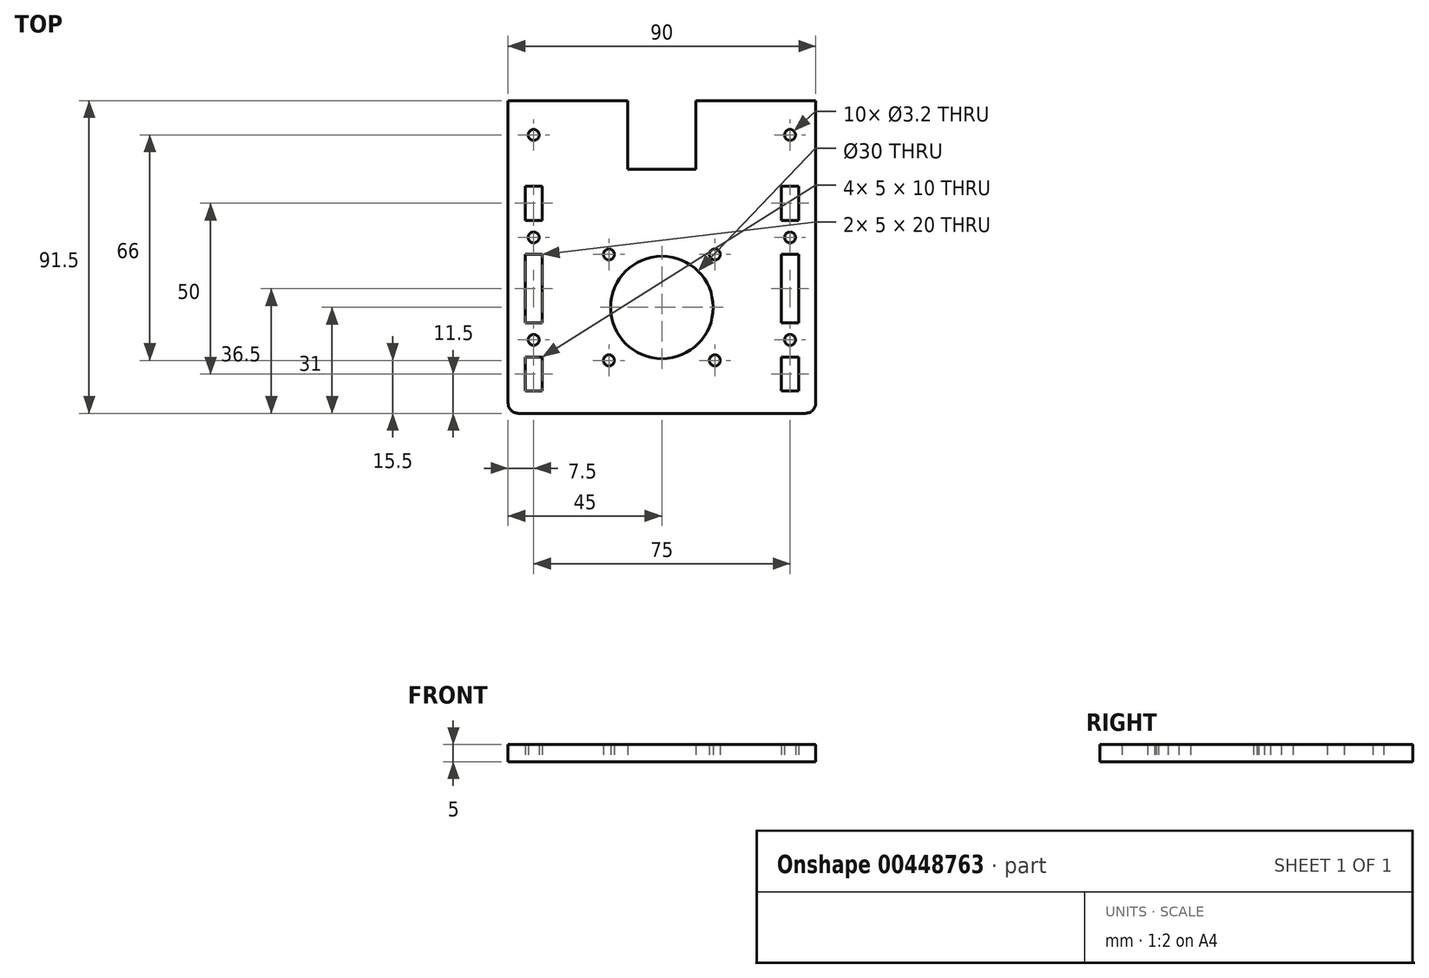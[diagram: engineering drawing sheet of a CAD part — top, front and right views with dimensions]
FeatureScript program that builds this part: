
annotation { "Feature Type Name" : "Feature", "Feature Type Description" : "" }
export const myFeature = defineFeature(function(context is Context, id is Id, definition is map)
    precondition{}
    {
        {
            assignVariable(context, id + "F0", {"name" : "thickness", "anyValue" : 5 * mm});
        }
        {
            var Q0;
            Q0=qCreatedBy(makeId("Top.planeOp"),FACE);
            var sketch = newSketch(context, id + "F1", { "sketchPlane" : qUnion([Q0])});
            skLineSegment(sketch, "E0", {"start": v(0, 0) * mm, "end": v(0, -20) * mm});
            skLineSegment(sketch, "E1", {"start": v(0, -20) * mm, "end": v(20, -20) * mm});
            skLineSegment(sketch, "E2", {"start": v(20, -20) * mm, "end": v(20, 0) * mm});
            skLineSegment(sketch, "E3", {"start": v(0, 0) * mm, "end": v(-35, 0) * mm});
            skCircle(sketch, "E4", {"center": v(10, -60.5) * mm, "radius": 15 * mm});
            skPoint(sketch, "E4.centerSnap0", {"position": v(10, -20) * mm});
            skCircle(sketch, "E5", {"center": v(25.5, -76) * mm, "radius": 1.6 * mm});
            skCircle(sketch, "E6.1.0", {"center": v(25.5, -45) * mm, "radius": 1.6 * mm});
            skCircle(sketch, "E6.2.0", {"center": v(-5.5, -45) * mm, "radius": 1.6 * mm});
            skCircle(sketch, "E6.3.0", {"center": v(-5.5, -76) * mm, "radius": 1.6 * mm});
            skLineSegment(sketch, "E7", {"start": v(-35, 0) * mm, "end": v(-35, -88.5) * mm});
            skLineSegment(sketch, "E8", {"start": v(-32, -91.5) * mm, "end": v(52, -91.5) * mm});
            skLineSegment(sketch, "E9", {"start": v(55, -88.5) * mm, "end": v(55, 0) * mm});
            skLineSegment(sketch, "E10", {"start": v(55, 0) * mm, "end": v(20, 0) * mm});
            skLineSegment(sketch, "E11.bottom", {"start": v(31, -39.5) * mm, "end": v(-11, -39.5) * mm, "construction": true});
            skLineSegment(sketch, "E11.top", {"start": v(31, -81.5) * mm, "end": v(-11, -81.5) * mm, "construction": true});
            skLineSegment(sketch, "E11.left", {"start": v(31, -39.5) * mm, "end": v(31, -81.5) * mm, "construction": true});
            skLineSegment(sketch, "E11.right", {"start": v(-11, -39.5) * mm, "end": v(-11, -81.5) * mm, "construction": true});
            skLineSegment(sketch, "E12.bottom", {"start": v(-30, -85) * mm, "end": v(-25, -85) * mm});
            skLineSegment(sketch, "E12.top", {"start": v(-30, -75) * mm, "end": v(-25, -75) * mm});
            skLineSegment(sketch, "E12.left", {"start": v(-30, -85) * mm, "end": v(-30, -75) * mm});
            skLineSegment(sketch, "E12.right", {"start": v(-25, -85) * mm, "end": v(-25, -75) * mm});
            skLineSegment(sketch, "E13.bottom", {"start": v(-30, -65) * mm, "end": v(-25, -65) * mm});
            skLineSegment(sketch, "E13.top", {"start": v(-30, -45) * mm, "end": v(-25, -45) * mm});
            skLineSegment(sketch, "E13.left", {"start": v(-30, -65) * mm, "end": v(-30, -45) * mm});
            skLineSegment(sketch, "E13.right", {"start": v(-25, -65) * mm, "end": v(-25, -45) * mm});
            skLineSegment(sketch, "E14.bottom", {"start": v(-30, -35) * mm, "end": v(-25, -35) * mm});
            skLineSegment(sketch, "E14.top", {"start": v(-30, -25) * mm, "end": v(-25, -25) * mm});
            skLineSegment(sketch, "E14.left", {"start": v(-30, -35) * mm, "end": v(-30, -25) * mm});
            skLineSegment(sketch, "E14.right", {"start": v(-25, -35) * mm, "end": v(-25, -25) * mm});
            skLineSegment(sketch, "E15", {"start": v(10, -91.5) * mm, "end": v(10, -20) * mm, "construction": true});
            skLineSegment(sketch, "E16.MirrorCS", {"start": v(50, -75) * mm, "end": v(45, -75) * mm});
            skLineSegment(sketch, "E17.MirrorCS", {"start": v(45, -85) * mm, "end": v(45, -75) * mm});
            skLineSegment(sketch, "E18.MirrorCS", {"start": v(50, -45) * mm, "end": v(45, -45) * mm});
            skLineSegment(sketch, "E19.MirrorCS", {"start": v(50, -65) * mm, "end": v(50, -45) * mm});
            skLineSegment(sketch, "E20.MirrorCS", {"start": v(50, -35) * mm, "end": v(45, -35) * mm});
            skLineSegment(sketch, "E21.MirrorCS", {"start": v(45, -35) * mm, "end": v(45, -25) * mm});
            skLineSegment(sketch, "E22.MirrorCS", {"start": v(50, -35) * mm, "end": v(50, -25) * mm});
            skLineSegment(sketch, "E23.MirrorCS", {"start": v(50, -25) * mm, "end": v(45, -25) * mm});
            skLineSegment(sketch, "E24.MirrorCS", {"start": v(45, -65) * mm, "end": v(45, -45) * mm});
            skLineSegment(sketch, "E25.MirrorCS", {"start": v(50, -65) * mm, "end": v(45, -65) * mm});
            skLineSegment(sketch, "E26.MirrorCS", {"start": v(50, -85) * mm, "end": v(50, -75) * mm});
            skLineSegment(sketch, "E27.MirrorCS", {"start": v(50, -85) * mm, "end": v(45, -85) * mm});
            skCircle(sketch, "E28", {"center": v(-27.5, -40) * mm, "radius": 1.6 * mm});
            skPoint(sketch, "E28.centerSnap0", {"position": v(-27.5, -35) * mm});
            skCircle(sketch, "E29", {"center": v(-27.5, -70) * mm, "radius": 1.6 * mm});
            skPoint(sketch, "E29.centerSnap0", {"position": v(-27.5, -65) * mm});
            skCircle(sketch, "E30.MirrorC", {"center": v(47.5, -40) * mm, "radius": 1.6 * mm});
            skCircle(sketch, "E31.MirrorC", {"center": v(47.5, -70) * mm, "radius": 1.6 * mm});
            skCircle(sketch, "E32", {"center": v(-27.5, -10) * mm, "radius": 1.6 * mm});
            skPoint(sketch, "E32.centerSnap0", {"position": v(0, -10) * mm});
            skCircle(sketch, "E33", {"center": v(47.5, -10) * mm, "radius": 1.6 * mm});
            skPoint(sketch, "E33.centerSnap0", {"position": v(20, -10) * mm});
            skLineSegment(sketch, "E34", {"start": v(-27.5, -10) * mm, "end": v(47.5, -10) * mm, "construction": true});
            skPoint(sketch, "E35", {"position": v(10, -10) * mm});
            skPoint(sketch, "E36.visualSharp", {"position": v(-35, -91.5) * mm});
            skArc(sketch, "E36.filletArc", {"start": v(-35, -88.5) * mm, "mid": v(-34.12, -90.62) * mm, "end": v(-32, -91.5) * mm});
            skPoint(sketch, "E37.visualSharp", {"position": v(55, -91.5) * mm});
            skArc(sketch, "E37.filletArc", {"start": v(52, -91.5) * mm, "mid": v(54.12, -90.62) * mm, "end": v(55, -88.5) * mm});
            skSolve(sketch);
        }
        {
            var Q0;
            Q0=qSketchRegion(id+"F1",true);
            extrude(context, id + "F2", {"entities" : qUnion([Q0]), "depth" : getVariable(context, 'thickness')});
        }
    });
